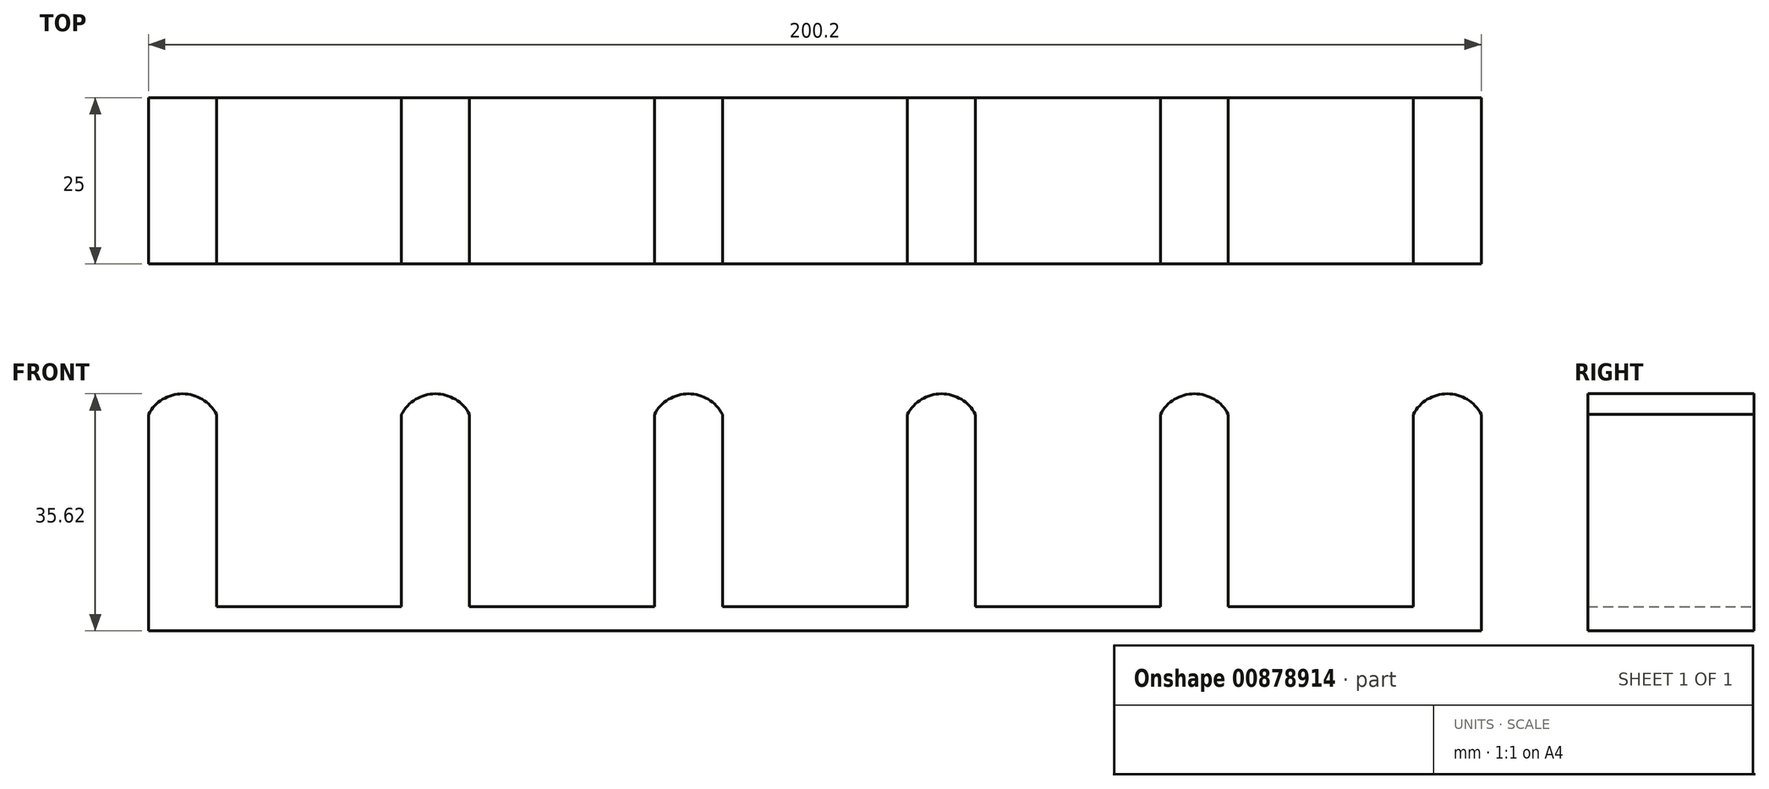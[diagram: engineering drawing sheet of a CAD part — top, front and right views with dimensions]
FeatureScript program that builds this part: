
annotation { "Feature Type Name" : "Feature", "Feature Type Description" : "" }
export const myFeature = defineFeature(function(context is Context, id is Id, definition is map)
    precondition{}
    {
        {
            var Q0;
            Q0=qCreatedBy(makeId("Front.planeOp"),FACE);
            var sketch = newSketch(context, id + "F0", { "sketchPlane" : qUnion([Q0])});
            skLineSegment(sketch, "E0", {"start": v(-43.37, 0) * mm, "end": v(55.58, 0) * mm});
            skLineSegment(sketch, "E1", {"start": v(-33, 32) * mm, "end": v(-33, -28.76) * mm, "construction": true});
            skLineSegment(sketch, "E2", {"start": v(-38.11, 0) * mm, "end": v(-38.11, 28.91) * mm});
            skLineSegment(sketch, "E3.MirrorCS", {"start": v(-27.9, 0) * mm, "end": v(-27.9, 28.91) * mm});
            skArc(sketch, "E4", {"start": v(-27.9, 28.91) * mm, "mid": v(-33, 32) * mm, "end": v(-38.11, 28.91) * mm});
            skLineSegment(sketch, "E5.1.0.0", {"start": v(-5.37, 0) * mm, "end": v(93.58, 0) * mm});
            skLineSegment(sketch, "E5.1.0.1", {"start": v(10.1, 0) * mm, "end": v(10.1, 28.91) * mm});
            skArc(sketch, "E5.1.0.2", {"start": v(10.1, 28.91) * mm, "mid": v(5, 32) * mm, "end": v(-0.11, 28.91) * mm});
            skLineSegment(sketch, "E5.1.0.3", {"start": v(-0.11, 0) * mm, "end": v(-0.11, 28.91) * mm});
            skLineSegment(sketch, "E5.1.0.4", {"start": v(5, 32) * mm, "end": v(5, -28.76) * mm, "construction": true});
            skLineSegment(sketch, "E5.2.0.0", {"start": v(32.63, 0) * mm, "end": v(131.58, 0) * mm});
            skLineSegment(sketch, "E5.2.0.1", {"start": v(48.1, 0) * mm, "end": v(48.1, 28.91) * mm});
            skArc(sketch, "E5.2.0.2", {"start": v(48.1, 28.91) * mm, "mid": v(43, 32) * mm, "end": v(37.89, 28.91) * mm});
            skLineSegment(sketch, "E5.2.0.3", {"start": v(37.89, 0) * mm, "end": v(37.89, 28.91) * mm});
            skLineSegment(sketch, "E5.2.0.4", {"start": v(43, 32) * mm, "end": v(43, -28.76) * mm, "construction": true});
            skLineSegment(sketch, "E5.direction1", {"start": v(-43.37, 0) * mm, "end": v(-5.37, 0) * mm, "construction": true});
            skLineSegment(sketch, "E6.bottom", {"start": v(-38.11, 0) * mm, "end": v(48.1, 0) * mm});
            skLineSegment(sketch, "E7.0.3.0", {"start": v(70.63, 0) * mm, "end": v(169.58, 0) * mm});
            skLineSegment(sketch, "E7.3.3.0", {"start": v(86.1, 0) * mm, "end": v(86.1, 28.91) * mm});
            skArc(sketch, "E7.6.3.0", {"start": v(86.1, 28.91) * mm, "mid": v(81, 32) * mm, "end": v(75.89, 28.91) * mm});
            skLineSegment(sketch, "E7.10.3.0", {"start": v(75.89, 0) * mm, "end": v(75.89, 28.91) * mm});
            skLineSegment(sketch, "E7.13.3.0", {"start": v(81, 32) * mm, "end": v(81, -28.76) * mm, "construction": true});
            skLineSegment(sketch, "E7.0.4.0", {"start": v(108.63, 0) * mm, "end": v(207.58, 0) * mm});
            skLineSegment(sketch, "E7.3.4.0", {"start": v(124.1, 0) * mm, "end": v(124.1, 28.91) * mm});
            skArc(sketch, "E7.6.4.0", {"start": v(124.1, 28.91) * mm, "mid": v(119, 32) * mm, "end": v(113.89, 28.91) * mm});
            skLineSegment(sketch, "E7.10.4.0", {"start": v(113.89, 0) * mm, "end": v(113.89, 28.91) * mm});
            skLineSegment(sketch, "E7.13.4.0", {"start": v(119, 32) * mm, "end": v(119, -28.76) * mm, "construction": true});
            skLineSegment(sketch, "E7.0.5.0", {"start": v(146.63, 0) * mm, "end": v(245.58, 0) * mm});
            skLineSegment(sketch, "E7.3.5.0", {"start": v(162.1, 0) * mm, "end": v(162.1, 28.91) * mm});
            skArc(sketch, "E7.6.5.0", {"start": v(162.1, 28.91) * mm, "mid": v(157, 32) * mm, "end": v(151.89, 28.91) * mm});
            skLineSegment(sketch, "E7.10.5.0", {"start": v(151.89, 0) * mm, "end": v(151.89, 28.91) * mm});
            skLineSegment(sketch, "E7.13.5.0", {"start": v(157, 32) * mm, "end": v(157, -28.76) * mm, "construction": true});
            skLineSegment(sketch, "E8.bottom", {"start": v(-38.11, 0) * mm, "end": v(162.1, 0) * mm});
            skLineSegment(sketch, "E8.top", {"start": v(-38.11, -3.62) * mm, "end": v(162.1, -3.62) * mm});
            skLineSegment(sketch, "E8.left", {"start": v(-38.11, 0) * mm, "end": v(-38.11, -3.62) * mm});
            skLineSegment(sketch, "E8.right", {"start": v(162.1, 0) * mm, "end": v(162.1, -3.62) * mm});
            skSolve(sketch);
        }
        {
            var Q0;
            {var subQ0=sQuery(id+"F0.wireOp",EDGE,"E2");Q0=makeQuery(id+"F0.imprint","IMPRINT",FACE,{"disambiguationData":[TD([[makeQuery(id+"F0.imprint","IMPRINT",EDGE,{"derivedFrom":subQ0}),-1.0]])]});}
            var Q1;
            {var subQ0=sQuery(id+"F0.wireOp",EDGE,"E5.1.0.1");Q1=makeQuery(id+"F0.imprint","IMPRINT",FACE,{"disambiguationData":[TD([[makeQuery(id+"F0.imprint","IMPRINT",EDGE,{"derivedFrom":subQ0}),1.0]])]});}
            var Q2;
            {var subQ0=sQuery(id+"F0.wireOp",EDGE,"E5.2.0.1");Q2=makeQuery(id+"F0.imprint","IMPRINT",FACE,{"disambiguationData":[TD([[makeQuery(id+"F0.imprint","IMPRINT",EDGE,{"derivedFrom":subQ0}),1.0]])]});}
            var Q3;
            Q3=makeQuery(id+"F0.imprint","IMPRINT",FACE,{"disambiguationData":[TD([[makeQuery(id+"F0.imprint","IMPRINT",EDGE,{"derivedFrom":sQuery(id+"F0.wireOp",EDGE,"E6.top")}),1.0]])]});
            var Q4;
            {var subQ0=sQuery(id+"F0.wireOp",EDGE,"E7.3.3.0");Q4=makeQuery(id+"F0.imprint","IMPRINT",FACE,{"disambiguationData":[TD([[makeQuery(id+"F0.imprint","IMPRINT",EDGE,{"derivedFrom":subQ0}),1.0]])]});}
            var Q5;
            {var subQ0=sQuery(id+"F0.wireOp",EDGE,"E7.3.4.0");Q5=makeQuery(id+"F0.imprint","IMPRINT",FACE,{"disambiguationData":[TD([[makeQuery(id+"F0.imprint","IMPRINT",EDGE,{"derivedFrom":subQ0}),1.0]])]});}
            var Q6;
            {var subQ0=sQuery(id+"F0.wireOp",EDGE,"E7.3.5.0");Q6=makeQuery(id+"F0.imprint","IMPRINT",FACE,{"disambiguationData":[TD([[makeQuery(id+"F0.imprint","IMPRINT",EDGE,{"derivedFrom":subQ0}),1.0]])]});}
            var Q7;
            Q7=makeQuery(id+"F0.imprint","IMPRINT",FACE,{"disambiguationData":[TD([[makeQuery(id+"F0.imprint","IMPRINT",EDGE,{"derivedFrom":sQuery(id+"F0.wireOp",EDGE,"E8.top")}),1.0]])]});
            extrude(context, id + "F1", {"entities" : qUnion([Q0, Q1, Q2, Q3, Q4, Q5, Q6, Q7]), "depth" : 25 * mm, "offsetDistance" : 25 * mm});
        }
    });
